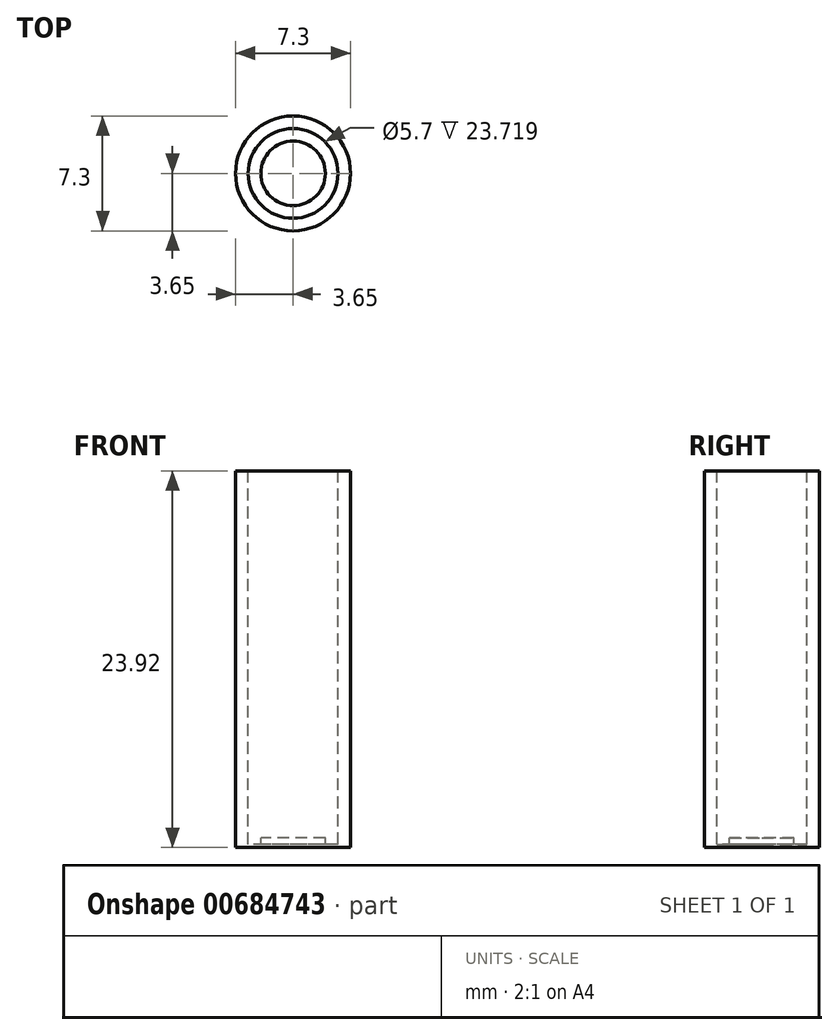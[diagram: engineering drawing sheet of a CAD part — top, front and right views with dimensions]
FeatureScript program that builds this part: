
annotation { "Feature Type Name" : "Feature", "Feature Type Description" : "" }
export const myFeature = defineFeature(function(context is Context, id is Id, definition is map)
    precondition{}
    {
        {
            var Q0;
            Q0=qCreatedBy(makeId("Front.planeOp"),FACE);
            var sketch = newSketch(context, id + "F0", { "sketchPlane" : qUnion([Q0])});
            skLineSegment(sketch, "E0", {"start": v(0, 0.6) * mm, "end": v(0, 0) * mm});
            skLineSegment(sketch, "E1", {"start": v(0, 0) * mm, "end": v(3.65, 0) * mm});
            skLineSegment(sketch, "E2", {"start": v(2.85, 23.92) * mm, "end": v(3.65, 23.92) * mm});
            skLineSegment(sketch, "E3", {"start": v(3.65, 23.92) * mm, "end": v(3.65, 0) * mm});
            skLineSegment(sketch, "E4", {"start": v(0, 0.6) * mm, "end": v(2.05, 0.6) * mm});
            skLineSegment(sketch, "E5", {"start": v(2.05, 0.6) * mm, "end": v(2.05, 0.2) * mm});
            skLineSegment(sketch, "E6", {"start": v(2.85, 23.92) * mm, "end": v(2.85, 0.2) * mm});
            skLineSegment(sketch, "E7", {"start": v(2.05, 0.2) * mm, "end": v(2.85, 0.2) * mm});
            skSolve(sketch);
        }
        {
            var Q0;
            Q0=qSketchRegion(id+"F0",true);
            var Q1;
            Q1=sQuery(id+"F0.wireOp",EDGE,"E0");
            revolve(context, id + "F1", {"entities" : qUnion([Q0]), "axis" : qUnion([Q1]), "revolveType" : RevolveType.FULL});
        }
    });
